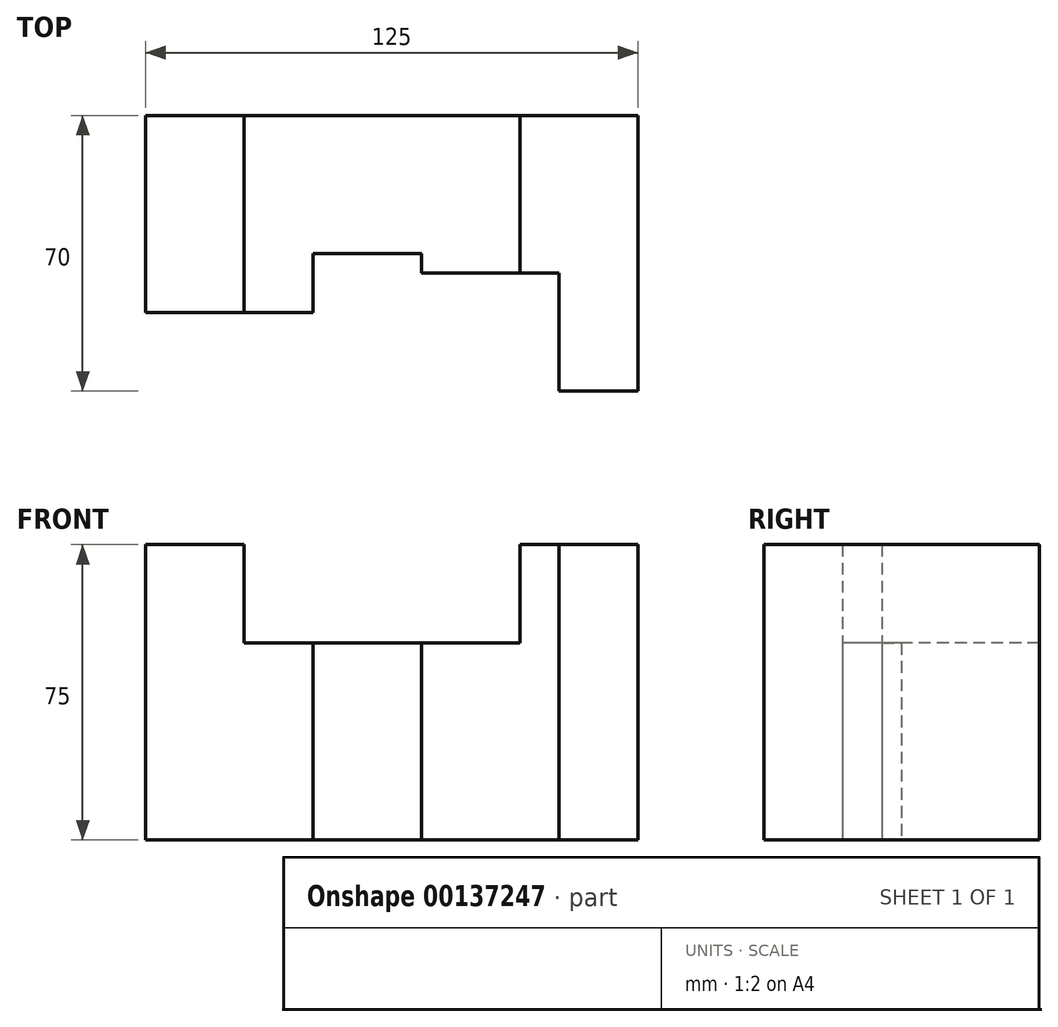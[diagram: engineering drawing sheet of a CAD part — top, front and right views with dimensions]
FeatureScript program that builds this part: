
annotation { "Feature Type Name" : "Feature", "Feature Type Description" : "" }
export const myFeature = defineFeature(function(context is Context, id is Id, definition is map)
    precondition{}
    {
        {
            var Q0;
            Q0=qCreatedBy(makeId("Top.planeOp"),FACE);
            var sketch = newSketch(context, id + "F0", { "sketchPlane" : qUnion([Q0])});
            skLineSegment(sketch, "E0", {"start": v(0, 0) * mm, "end": v(0, 50) * mm});
            skLineSegment(sketch, "E1", {"start": v(0, 50) * mm, "end": v(25, 50) * mm});
            skLineSegment(sketch, "E2", {"start": v(25, 50) * mm, "end": v(25, 0) * mm});
            skLineSegment(sketch, "E3", {"start": v(25, 0) * mm, "end": v(0, 0) * mm});
            skLineSegment(sketch, "E4", {"start": v(25, 50) * mm, "end": v(95, 50) * mm});
            skLineSegment(sketch, "E5", {"start": v(95, 50) * mm, "end": v(95, 10) * mm});
            skLineSegment(sketch, "E6", {"start": v(95, 10) * mm, "end": v(70, 10) * mm});
            skLineSegment(sketch, "E7", {"start": v(70, 10) * mm, "end": v(70, 15) * mm});
            skLineSegment(sketch, "E8", {"start": v(70, 15) * mm, "end": v(42.5, 15) * mm});
            skLineSegment(sketch, "E9", {"start": v(42.5, 15) * mm, "end": v(42.5, 0) * mm});
            skLineSegment(sketch, "E10", {"start": v(42.5, 0) * mm, "end": v(25, 0) * mm});
            skLineSegment(sketch, "E11", {"start": v(95, 50) * mm, "end": v(125, 50) * mm});
            skLineSegment(sketch, "E12", {"start": v(125, 50) * mm, "end": v(125, -20) * mm});
            skLineSegment(sketch, "E13", {"start": v(125, -20) * mm, "end": v(105, -20) * mm});
            skLineSegment(sketch, "E14", {"start": v(105, -20) * mm, "end": v(105, 10) * mm});
            skLineSegment(sketch, "E15", {"start": v(105, 10) * mm, "end": v(95, 10) * mm});
            skSolve(sketch);
        }
        {
            var Q0;
            Q0=makeQuery(id+"F0.imprint","IMPRINT",FACE,{"disambiguationData":[TD([[makeQuery(id+"F0.imprint","IMPRINT",EDGE,{"derivedFrom":sQuery(id+"F0.wireOp",EDGE,"E0")}),-1.0]])]});
            var Q1;
            Q1=makeQuery(id+"F0.imprint","IMPRINT",FACE,{"disambiguationData":[TD([[makeQuery(id+"F0.imprint","IMPRINT",EDGE,{"derivedFrom":sQuery(id+"F0.wireOp",EDGE,"E5")}),1.0]])]});
            extrude(context, id + "F1", {"entities" : qUnion([Q0, Q1]), "depth" : (15 * 5) * mm});
        }
        {
            var Q0;
            Q0=makeQuery(id+"F0.imprint","IMPRINT",FACE,{"disambiguationData":[TD([[makeQuery(id+"F0.imprint","IMPRINT",EDGE,{"derivedFrom":sQuery(id+"F0.wireOp",EDGE,"E2")}),1.0]])]});
            extrude(context, id + "F2", {"entities" : qUnion([Q0]), "operationType" : NewBodyOperationType.ADD, "depth" : 50 * mm});
        }
    });
